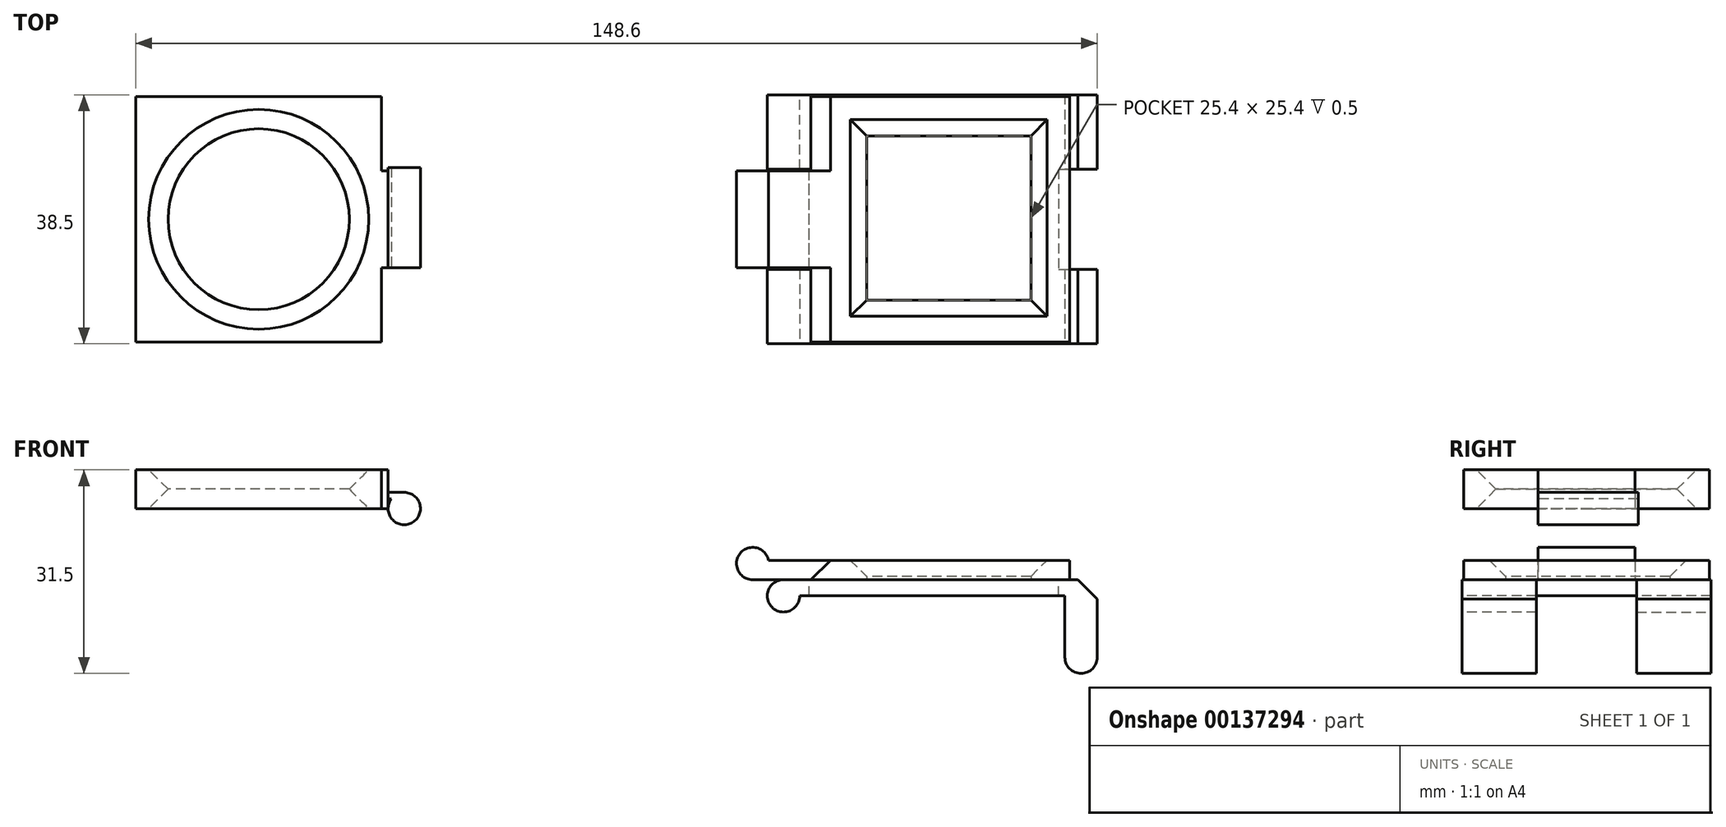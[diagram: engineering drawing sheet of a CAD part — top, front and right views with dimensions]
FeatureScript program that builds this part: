
annotation { "Feature Type Name" : "Feature", "Feature Type Description" : "" }
export const myFeature = defineFeature(function(context is Context, id is Id, definition is map)
    precondition{}
    {
        {
            var Q0;
            Q0=qCreatedBy(makeId("Top.planeOp"),FACE);
            var sketch = newSketch(context, id + "F0", { "sketchPlane" : qUnion([Q0])});
            skLineSegment(sketch, "E0.bottom", {"start": v(20, 19) * mm, "end": v(-20, 19) * mm});
            skLineSegment(sketch, "E0.top", {"start": v(20, -19) * mm, "end": v(-20, -19) * mm});
            skLineSegment(sketch, "E0.left", {"start": v(20, 19) * mm, "end": v(20, -19) * mm});
            skLineSegment(sketch, "E0.right", {"start": v(-20, 19) * mm, "end": v(-20, -19) * mm});
            skPoint(sketch, "E0.middle", {"position": v(0, 0) * mm});
            skLineSegment(sketch, "E1.bottom", {"start": v(-20, 7.5) * mm, "end": v(-29, 7.5) * mm});
            skLineSegment(sketch, "E1.top", {"start": v(-20, -7.5) * mm, "end": v(-29, -7.5) * mm});
            skLineSegment(sketch, "E1.left", {"start": v(-20, 7.5) * mm, "end": v(-20, -7.5) * mm});
            skLineSegment(sketch, "E1.right", {"start": v(-29, 7.5) * mm, "end": v(-29, -7.5) * mm});
            skLineSegment(sketch, "E2.bottom", {"start": v(-11.4, 12.9) * mm, "end": v(14, 12.9) * mm});
            skLineSegment(sketch, "E2.top", {"start": v(-11.4, -12.5) * mm, "end": v(14, -12.5) * mm});
            skLineSegment(sketch, "E2.left", {"start": v(-11.4, 12.9) * mm, "end": v(-11.4, -12.5) * mm});
            skLineSegment(sketch, "E2.right", {"start": v(14, 12.9) * mm, "end": v(14, -12.5) * mm});
            skSolve(sketch);
        }
        {
            var Q0;
            {var subQ1=sQuery(id+"F0.wireOp",EDGE,"E0.bottom");Q0=makeQuery(id+"F0.imprint","IMPRINT",FACE,{"disambiguationData":[TD([[makeQuery(id+"F0.imprint","IMPRINT",EDGE,{"derivedFrom":subQ1}),1.0]])]});}
            var Q1;
            Q1=makeQuery(id+"F0.imprint","IMPRINT",FACE,{"disambiguationData":[TD([[makeQuery(id+"F0.imprint","IMPRINT",EDGE,{"derivedFrom":sQuery(id+"F0.wireOp",EDGE,"E1.bottom")}),1.0]])]});
            extrude(context, id + "F1", {"entities" : qUnion([Q0, Q1]), "depth" : 3 * mm});
        }
        {
            var Q0;
            {var subQ0=sQuery(id+"F0.wireOp",EDGE,"E0.right");Q0=makeQuery(id+"F1.opExtrude","CAP_EDGE",EDGE,{"disambiguationData":[OSD([subQ0]),TDD([makeQuery(id+"F0.imprint","IMPRINT",EDGE,{"disambiguationData":[TD([[makeQuery(id+"F0.imprint","INTERSECT",VERTEX,{"derivedFrom":[sQuery(id+"F0.wireOp",EDGE,"E0.top"),subQ0]}),1.0]])],"derivedFrom":subQ0})])],"isStart":false});}
            var Q1;
            {var subQ0=sQuery(id+"F0.wireOp",EDGE,"E0.right");Q1=makeQuery(id+"F1.opExtrude","CAP_EDGE",EDGE,{"disambiguationData":[OSD([subQ0]),TDD([makeQuery(id+"F0.imprint","IMPRINT",EDGE,{"disambiguationData":[TD([[makeQuery(id+"F0.imprint","INTERSECT",VERTEX,{"derivedFrom":[sQuery(id+"F0.wireOp",EDGE,"E0.bottom"),subQ0]}),-1.0]])],"derivedFrom":subQ0})])],"isStart":false});}
            chamfer(context, id + "F2", {"entities" : qUnion([Q0, Q1]), "width" : 3 * mm});
        }
        {
            var Q0;
            Q0=makeQuery(id+"F1.opExtrude","CAP_EDGE",EDGE,{"disambiguationData":[OSD([sQuery(id+"F0.wireOp",EDGE,"E2.bottom")])],"isStart":false});
            var Q1;
            Q1=makeQuery(id+"F1.opExtrude","CAP_EDGE",EDGE,{"disambiguationData":[OSD([sQuery(id+"F0.wireOp",EDGE,"E2.right")])],"isStart":false});
            var Q2;
            Q2=makeQuery(id+"F1.opExtrude","CAP_EDGE",EDGE,{"disambiguationData":[OSD([sQuery(id+"F0.wireOp",EDGE,"E2.top")])],"isStart":false});
            var Q3;
            Q3=makeQuery(id+"F1.opExtrude","CAP_EDGE",EDGE,{"disambiguationData":[OSD([sQuery(id+"F0.wireOp",EDGE,"E2.left")])],"isStart":false});
            chamfer(context, id + "F3", {"entities" : qUnion([Q0, Q1, Q2, Q3]), "width" : 2.5 * mm, "tangentPropagation" : true});
        }
        {
            var Q0;
            Q0=makeQuery(id+"F1.opExtrude","SWEPT_FACE",FACE,{"disambiguationData":[OSD([sQuery(id+"F0.wireOp",EDGE,"E1.top")])]});
            var sketch = newSketch(context, id + "F4", { "sketchPlane" : qUnion([Q0])});
            skCircle(sketch, "E3", {"center": v(-29, 2.5) * mm, "radius": 2.5 * mm});
            skSolve(sketch);
        }
        {
            var Q0;
            Q0 = qSketchRegion(id + "F4", true);
            extrude(context, id + "F5", {"entities" : qUnion([Q0]), "operationType" : NewBodyOperationType.ADD, "oppositeDirection" : true, "depth" : 15 * mm});
        }
        {
            var Q0;
            Q0=qCreatedBy(makeId("Top.planeOp"),FACE);
            var sketch = newSketch(context, id + "F6", { "sketchPlane" : qUnion([Q0])});
            skLineSegment(sketch, "E4.bottom", {"start": v(-24.25, 19.25) * mm, "end": v(24.25, 19.25) * mm});
            skLineSegment(sketch, "E4.top", {"start": v(-24.25, -19.25) * mm, "end": v(24.25, -19.25) * mm});
            skLineSegment(sketch, "E4.left", {"start": v(-24.25, 19.25) * mm, "end": v(-24.25, -19.25) * mm});
            skLineSegment(sketch, "E4.right", {"start": v(24.25, 19.25) * mm, "end": v(24.25, -19.25) * mm});
            skPoint(sketch, "E4.middle", {"position": v(0, 0) * mm});
            skLineSegment(sketch, "E5.bottom", {"start": v(18.25, 7.75) * mm, "end": v(30.25, 7.75) * mm});
            skLineSegment(sketch, "E5.top", {"start": v(18.25, -7.75) * mm, "end": v(30.25, -7.75) * mm});
            skLineSegment(sketch, "E5.left", {"start": v(18.25, 7.75) * mm, "end": v(18.25, -7.75) * mm});
            skLineSegment(sketch, "E5.right", {"start": v(30.25, 7.75) * mm, "end": v(30.25, -7.75) * mm});
            skPoint(sketch, "E5.middle", {"position": v(24.25, 0) * mm});
            skLineSegment(sketch, "E6.bottom", {"start": v(-20.25, -7.75) * mm, "end": v(-28.25, -7.75) * mm});
            skLineSegment(sketch, "E6.top", {"start": v(-20.25, 7.75) * mm, "end": v(-28.25, 7.75) * mm});
            skLineSegment(sketch, "E6.left", {"start": v(-20.25, -7.75) * mm, "end": v(-20.25, 7.75) * mm});
            skLineSegment(sketch, "E6.right", {"start": v(-28.25, -7.75) * mm, "end": v(-28.25, 7.75) * mm});
            skPoint(sketch, "E6.middle", {"position": v(-24.25, 0) * mm});
            skLineSegment(sketch, "E7", {"start": v(19.25, 19.25) * mm, "end": v(19.25, -19.25) * mm});
            skSolve(sketch);
        }
        {
            var Q0;
            {var subQ6=sQuery(id+"F6.wireOp",EDGE,"E5.left");Q0=makeQuery(id+"F6.imprint","IMPRINT",FACE,{"disambiguationData":[TD([[makeQuery(id+"F6.imprint","IMPRINT",EDGE,{"derivedFrom":subQ6}),-1.0]])]});}
            var Q1;
            {var subQ0=sQuery(id+"F6.wireOp",EDGE,"E4.right");var subQ1=sQuery(id+"F6.wireOp",EDGE,"E4.top");var subQ2=makeQuery(id+"F6.imprint","INTERSECT",VERTEX,{"derivedFrom":[subQ1,subQ0]});Q1=makeQuery(id+"F6.imprint","IMPRINT",FACE,{"disambiguationData":[TD([[makeQuery(id+"F6.imprint","IMPRINT",EDGE,{"disambiguationData":[TD([[subQ2,1.0]])],"derivedFrom":subQ1}),1.0]])]});}
            var Q2;
            {var subQ0=sQuery(id+"F6.wireOp",EDGE,"E4.right");var subQ1=sQuery(id+"F6.wireOp",EDGE,"E4.bottom");var subQ2=makeQuery(id+"F6.imprint","INTERSECT",VERTEX,{"derivedFrom":[subQ1,subQ0]});Q2=makeQuery(id+"F6.imprint","IMPRINT",FACE,{"disambiguationData":[TD([[makeQuery(id+"F6.imprint","IMPRINT",EDGE,{"disambiguationData":[TD([[subQ2,1.0]])],"derivedFrom":subQ1}),-1.0]])]});}
            extrude(context, id + "F7", {"entities" : qUnion([Q0, Q1, Q2]), "oppositeDirection" : true, "depth" : 2.5 * mm});
        }
        {
            var Q0;
            {var subQ0=sQuery(id+"F6.wireOp",EDGE,"E4.right");var subQ1=sQuery(id+"F6.wireOp",EDGE,"E4.top");var subQ2=makeQuery(id+"F6.imprint","INTERSECT",VERTEX,{"derivedFrom":[subQ1,subQ0]});Q0=makeQuery(id+"F6.imprint","IMPRINT",FACE,{"disambiguationData":[TD([[makeQuery(id+"F6.imprint","IMPRINT",EDGE,{"disambiguationData":[TD([[subQ2,1.0]])],"derivedFrom":subQ1}),1.0]])]});}
            var Q1;
            {var subQ0=sQuery(id+"F6.wireOp",EDGE,"E4.right");var subQ1=sQuery(id+"F6.wireOp",EDGE,"E4.bottom");var subQ2=makeQuery(id+"F6.imprint","INTERSECT",VERTEX,{"derivedFrom":[subQ1,subQ0]});Q1=makeQuery(id+"F6.imprint","IMPRINT",FACE,{"disambiguationData":[TD([[makeQuery(id+"F6.imprint","IMPRINT",EDGE,{"disambiguationData":[TD([[subQ2,1.0]])],"derivedFrom":subQ1}),-1.0]])]});}
            extrude(context, id + "F8", {"entities" : qUnion([Q0, Q1]), "operationType" : NewBodyOperationType.ADD, "oppositeDirection" : true, "depth" : 12 * mm});
        }
        {
            var Q0;
            {var subQ0=sQuery(id+"F6.wireOp",EDGE,"E4.top");Q0=makeQuery(id+"F8.boolean.opBoolean","MERGE",FACE,{"derivedFrom":[makeQuery(id+"F7.opExtrude","SWEPT_FACE",FACE,{"disambiguationData":[OSD([subQ0])]}),makeQuery(id+"F8.opExtrude","SWEPT_FACE",FACE,{"disambiguationData":[OSD([subQ0])]})]});}
            var sketch = newSketch(context, id + "F9", { "sketchPlane" : qUnion([Q0])});
            skCircle(sketch, "E8", {"center": v(21.75, -12) * mm, "radius": 2.5 * mm});
            skSolve(sketch);
        }
        {
            var Q0;
            Q0 = qSketchRegion(id + "F9", true);
            extrude(context, id + "F10", {"entities" : qUnion([Q0]), "operationType" : NewBodyOperationType.ADD, "oppositeDirection" : true, "depth" : 11.5 * mm});
        }
        {
            var Q0;
            {var subQ0=sQuery(id+"F6.wireOp",EDGE,"E4.bottom");Q0=makeQuery(id+"F8.boolean.opBoolean","MERGE",FACE,{"derivedFrom":[makeQuery(id+"F7.opExtrude","SWEPT_FACE",FACE,{"disambiguationData":[OSD([subQ0])]}),makeQuery(id+"F8.opExtrude","SWEPT_FACE",FACE,{"disambiguationData":[OSD([subQ0])]})]});}
            var sketch = newSketch(context, id + "F11", { "sketchPlane" : qUnion([Q0])});
            skCircle(sketch, "E9", {"center": v(-21.75, -12) * mm, "radius": 2.5 * mm});
            skSolve(sketch);
        }
        {
            var Q0;
            Q0 = qSketchRegion(id + "F11", true);
            extrude(context, id + "F12", {"entities" : qUnion([Q0]), "operationType" : NewBodyOperationType.ADD, "oppositeDirection" : true, "depth" : 11.5 * mm});
        }
        {
            var Q0;
            {var subQ0=sQuery(id+"F6.wireOp",EDGE,"E4.right");Q0=makeQuery(id+"F7.opExtrude","CAP_EDGE",EDGE,{"disambiguationData":[OSD([subQ0]),TDD([makeQuery(id+"F6.imprint","IMPRINT",EDGE,{"disambiguationData":[TD([[makeQuery(id+"F6.imprint","INTERSECT",VERTEX,{"derivedFrom":[sQuery(id+"F6.wireOp",EDGE,"E4.top"),subQ0]}),1.0]])],"derivedFrom":subQ0})])],"isStart":true});}
            var Q1;
            {var subQ0=sQuery(id+"F6.wireOp",EDGE,"E4.right");Q1=makeQuery(id+"F7.opExtrude","CAP_EDGE",EDGE,{"disambiguationData":[OSD([subQ0]),TDD([makeQuery(id+"F6.imprint","IMPRINT",EDGE,{"disambiguationData":[TD([[makeQuery(id+"F6.imprint","INTERSECT",VERTEX,{"derivedFrom":[sQuery(id+"F6.wireOp",EDGE,"E4.bottom"),subQ0]}),-1.0]])],"derivedFrom":subQ0})])],"isStart":true});}
            chamfer(context, id + "F13", {"entities" : qUnion([Q0, Q1]), "width" : 3 * mm});
        }
        {
            var Q0;
            {var subQ0=sQuery(id+"F6.wireOp",EDGE,"E4.top");Q0=makeQuery(id+"F10.boolean.opBoolean","MERGE",FACE,{"derivedFrom":[makeQuery(id+"F8.boolean.opBoolean","MERGE",FACE,{"derivedFrom":[makeQuery(id+"F7.opExtrude","SWEPT_FACE",FACE,{"disambiguationData":[OSD([subQ0])]}),makeQuery(id+"F8.opExtrude","SWEPT_FACE",FACE,{"disambiguationData":[OSD([subQ0])]})]}),makeQuery(id+"F10.opExtrude","CAP_FACE",FACE,{"disambiguationData":[OSD([sQuery(id+"F9.wireOp",EDGE,"E8")])],"isStart":true})]});}
            var sketch = newSketch(context, id + "F14", { "sketchPlane" : qUnion([Q0])});
            skCircle(sketch, "E10", {"center": v(-24.25, -2.5) * mm, "radius": 2.5 * mm});
            skSolve(sketch);
        }
        {
            var Q0;
            Q0 = qSketchRegion(id + "F14", true);
            extrude(context, id + "F15", {"entities" : qUnion([Q0]), "operationType" : NewBodyOperationType.ADD, "oppositeDirection" : true, "depth" : 11.5 * mm});
        }
        {
            var Q0;
            {var subQ0=sQuery(id+"F6.wireOp",EDGE,"E4.bottom");Q0=makeQuery(id+"F12.boolean.opBoolean","MERGE",FACE,{"derivedFrom":[makeQuery(id+"F8.boolean.opBoolean","MERGE",FACE,{"derivedFrom":[makeQuery(id+"F7.opExtrude","SWEPT_FACE",FACE,{"disambiguationData":[OSD([subQ0])]}),makeQuery(id+"F8.opExtrude","SWEPT_FACE",FACE,{"disambiguationData":[OSD([subQ0])]})]}),makeQuery(id+"F12.opExtrude","CAP_FACE",FACE,{"disambiguationData":[OSD([sQuery(id+"F11.wireOp",EDGE,"E9")])],"isStart":true})]});}
            var sketch = newSketch(context, id + "F16", { "sketchPlane" : qUnion([Q0])});
            skCircle(sketch, "E11", {"center": v(24.25, -2.5) * mm, "radius": 2.5 * mm});
            skSolve(sketch);
        }
        {
            var Q0;
            Q0 = qSketchRegion(id + "F16", true);
            extrude(context, id + "F17", {"entities" : qUnion([Q0]), "operationType" : NewBodyOperationType.ADD, "oppositeDirection" : true, "depth" : 11.5 * mm});
        }
        {
            var Q0;
            Q0=makeQuery(id+"F1.opExtrude","SWEPT_BODY",BODY,{"disambiguationData":[OSD([sQuery(id+"F0.wireOp",EDGE,"E0.bottom"),sQuery(id+"F0.wireOp",EDGE,"E0.top"),sQuery(id+"F0.wireOp",EDGE,"E0.left"),sQuery(id+"F0.wireOp",EDGE,"E0.right"),sQuery(id+"F0.wireOp",EDGE,"E1.bottom"),sQuery(id+"F0.wireOp",EDGE,"E1.top"),sQuery(id+"F0.wireOp",EDGE,"E1.right"),sQuery(id+"F0.wireOp",EDGE,"E2.bottom"),sQuery(id+"F0.wireOp",EDGE,"E2.top"),sQuery(id+"F0.wireOp",EDGE,"E2.left"),sQuery(id+"F0.wireOp",EDGE,"E2.right")])]});
            transform(context, id + "F18", {"entities" : qUnion([Q0]), "transformType" : TransformType.TRANSLATION_3D, "dx" : 50.84 * mm, "dy" : 0 * mm, "dz" : -11 * mm, "makeCopy" : false});
        }
        {
            var Q0;
            Q0=qCreatedBy(makeId("Top.planeOp"),FACE);
            var sketch = newSketch(context, id + "F19", { "sketchPlane" : qUnion([Q0])});
            skLineSegment(sketch, "E12.bottom", {"start": v(-35.51, 19) * mm, "end": v(-73.51, 19) * mm});
            skLineSegment(sketch, "E12.top", {"start": v(-35.51, -19) * mm, "end": v(-73.51, -19) * mm});
            skLineSegment(sketch, "E12.left", {"start": v(-35.51, 19) * mm, "end": v(-35.51, -19) * mm});
            skLineSegment(sketch, "E12.right", {"start": v(-73.51, 19) * mm, "end": v(-73.51, -19) * mm});
            skPoint(sketch, "E12.middle", {"position": v(-54.51, 0) * mm});
            skCircle(sketch, "E13", {"center": v(-54.51, 0) * mm, "radius": 14 * mm});
            skLineSegment(sketch, "E14.bottom", {"start": v(-34.51, 7.5) * mm, "end": v(-36.51, 7.5) * mm});
            skLineSegment(sketch, "E14.top", {"start": v(-34.51, -7.5) * mm, "end": v(-36.51, -7.5) * mm});
            skLineSegment(sketch, "E14.left", {"start": v(-34.51, 7.5) * mm, "end": v(-34.51, -7.5) * mm});
            skLineSegment(sketch, "E14.right", {"start": v(-36.51, 7.5) * mm, "end": v(-36.51, -7.5) * mm});
            skPoint(sketch, "E14.middle", {"position": v(-35.51, 0) * mm});
            skSolve(sketch);
        }
        {
            var Q0;
            Q0 = qSketchRegion(id + "F19", true);
            extrude(context, id + "F20", {"entities" : qUnion([Q0]), "depth" : 6 * mm});
        }
        {
            var Q0;
            Q0=makeQuery(id+"F20.opExtrude","SWEPT_FACE",FACE,{"disambiguationData":[OSD([sQuery(id+"F19.wireOp",EDGE,"E14.top")])]});
            var sketch = newSketch(context, id + "F21", { "sketchPlane" : qUnion([Q0])});
            skLineSegment(sketch, "E15.bottom", {"start": v(-34.51, 0) * mm, "end": v(-32.01, 0) * mm});
            skLineSegment(sketch, "E15.top", {"start": v(-34.51, 1) * mm, "end": v(-32.01, 1) * mm});
            skLineSegment(sketch, "E15.left", {"start": v(-34.51, 0) * mm, "end": v(-34.51, 1) * mm});
            skLineSegment(sketch, "E15.right", {"start": v(-32.01, 0) * mm, "end": v(-32.01, 1) * mm});
            skCircle(sketch, "E16", {"center": v(-32.01, -1.5) * mm, "radius": 2.5 * mm});
            skPoint(sketch, "E16.second.point", {"position": v(-32.01, -4) * mm});
            skPoint(sketch, "E16.second.point.positionSnap0", {"position": v(-32.01, 0.5) * mm});
            skPoint(sketch, "E16.third.point", {"position": v(-30.01, 0) * mm});
            skSolve(sketch);
        }
        {
            var Q0;
            {var subQ4=sQuery(id+"F21.wireOp",EDGE,"E15.top");Q0=makeQuery(id+"F21.imprint","IMPRINT",FACE,{"disambiguationData":[TD([[makeQuery(id+"F21.imprint","IMPRINT",EDGE,{"derivedFrom":subQ4}),-1.0]])]});}
            var Q1;
            {var subQ0=sQuery(id+"F21.wireOp",EDGE,"E15.right");Q1=makeQuery(id+"F21.imprint","IMPRINT",FACE,{"disambiguationData":[TD([[makeQuery(id+"F21.imprint","IMPRINT",EDGE,{"derivedFrom":subQ0}),-1.0]])]});}
            var Q2;
            {var subQ0=sQuery(id+"F21.wireOp",EDGE,"E15.right");Q2=makeQuery(id+"F21.imprint","IMPRINT",FACE,{"disambiguationData":[TD([[makeQuery(id+"F21.imprint","IMPRINT",EDGE,{"derivedFrom":subQ0}),1.0]])]});}
            extrude(context, id + "F22", {"entities" : qUnion([Q0, Q1, Q2]), "oppositeDirection" : true, "depth" : 15.5 * mm});
        }
        {
            var Q0;
            Q0=makeQuery(id+"F20.opExtrude","CAP_EDGE",EDGE,{"disambiguationData":[OSD([sQuery(id+"F19.wireOp",EDGE,"E13")])],"isStart":false});
            var Q1;
            Q1=makeQuery(id+"F20.opExtrude","CAP_EDGE",EDGE,{"disambiguationData":[OSD([sQuery(id+"F19.wireOp",EDGE,"E13")])],"isStart":true});
            chamfer(context, id + "F23", {"entities" : qUnion([Q0, Q1]), "width" : 3 * mm, "tangentPropagation" : true});
        }
        {
            var Q0;
            Q0=makeQuery(id+"F22.opExtrude","SWEPT_BODY",BODY,{"disambiguationData":[OSD([sQuery(id+"F21.wireOp",EDGE,"E15.bottom"),sQuery(id+"F21.wireOp",EDGE,"E15.top"),sQuery(id+"F21.wireOp",EDGE,"E15.left"),sQuery(id+"F21.wireOp",EDGE,"E16")])]});
            var Q1;
            Q1=makeQuery(id+"F22.opExtrude","SWEPT_FACE",FACE,{"disambiguationData":[OSD([sQuery(id+"F21.wireOp",EDGE,"E15.top")])]});
            transform(context, id + "F24", {"entities" : qUnion([Q0]), "transformType" : TransformType.TRANSLATION_DISTANCE, "transformDirection" : qUnion([Q1]), "distance" : 1.5 * mm, "makeCopy" : false});
        }
    });
